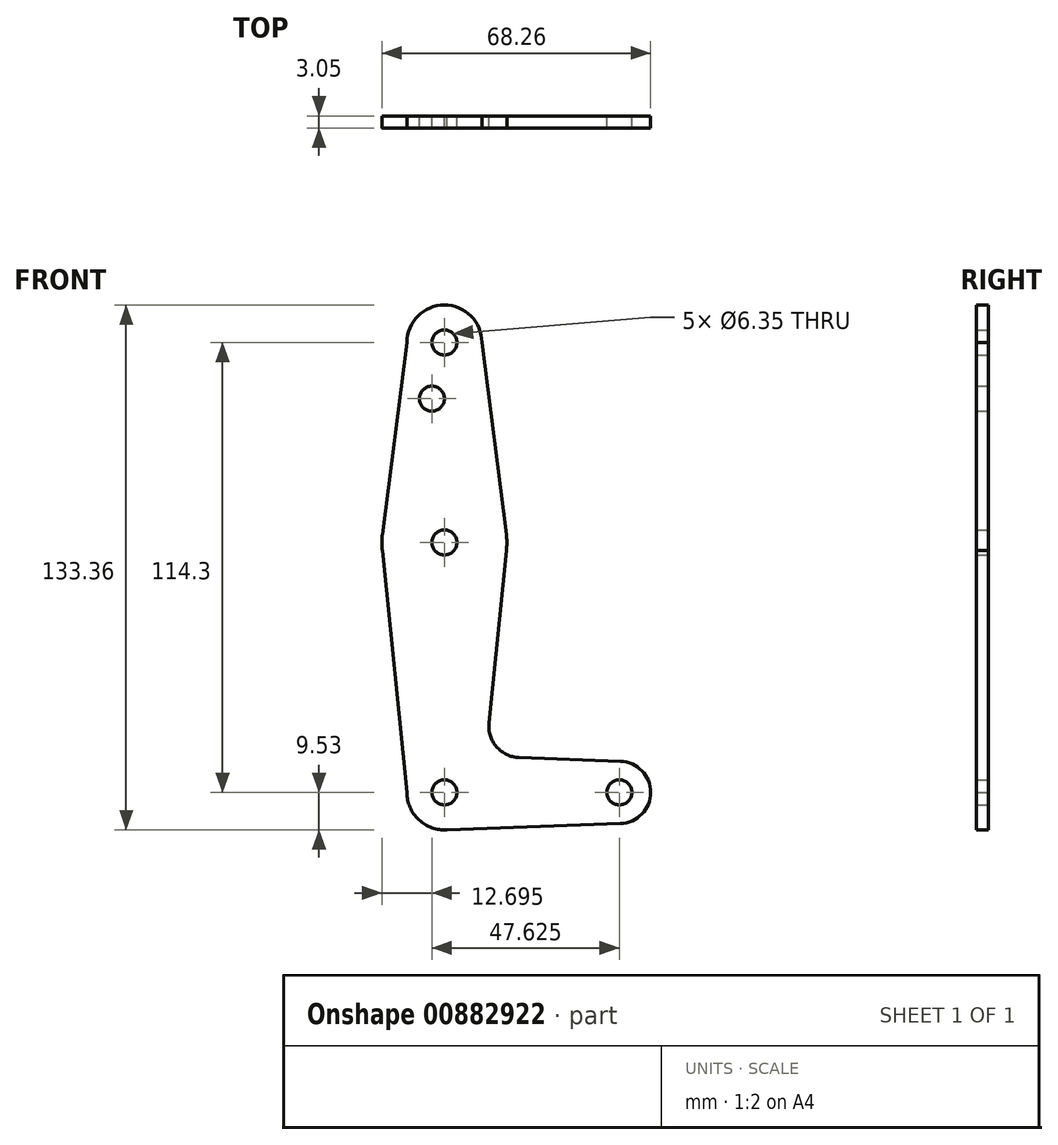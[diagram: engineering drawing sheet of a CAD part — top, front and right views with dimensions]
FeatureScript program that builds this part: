
annotation { "Feature Type Name" : "Feature", "Feature Type Description" : "" }
export const myFeature = defineFeature(function(context is Context, id is Id, definition is map)
    precondition{}
    {
        {
            var Q0;
            Q0=qCreatedBy(makeId("Front.planeOp"),FACE);
            var sketch = newSketch(context, id + "F0", { "sketchPlane" : qUnion([Q0])});
            skLineSegment(sketch, "E0", {"start": v(0, 0) * mm, "end": v(0, 114.3) * mm, "construction": true});
            skLineSegment(sketch, "E1", {"start": v(0, 0) * mm, "end": v(44.45, 0) * mm, "construction": true});
            skCircle(sketch, "E2", {"center": v(0, 63.5) * mm, "radius": 15.88 * mm});
            skCircle(sketch, "E3", {"center": v(0, 0) * mm, "radius": 9.53 * mm});
            skCircle(sketch, "E4", {"center": v(44.45, 0) * mm, "radius": 7.94 * mm});
            skCircle(sketch, "E5", {"center": v(0, 114.3) * mm, "radius": 9.53 * mm});
            skLineSegment(sketch, "E6", {"start": v(0, -9.52) * mm, "end": v(44.73, -7.93) * mm});
            skLineSegment(sketch, "E7", {"start": v(18.97, 8.85) * mm, "end": v(44.73, 7.93) * mm});
            skLineSegment(sketch, "E8", {"start": v(9.52, 114.3) * mm, "end": v(15.75, 65.5) * mm});
            skLineSegment(sketch, "E9", {"start": v(-9.52, 114.3) * mm, "end": v(-15.75, 65.5) * mm});
            skLineSegment(sketch, "E10", {"start": v(-15.75, 61.5) * mm, "end": v(-9.53, 0) * mm});
            skLineSegment(sketch, "E11", {"start": v(15.75, 61.5) * mm, "end": v(11.34, 17.6) * mm});
            skCircle(sketch, "E12", {"center": v(-3.17, 100.03) * mm, "radius": 3.18 * mm});
            skCircle(sketch, "E13", {"center": v(0, 114.3) * mm, "radius": 3.18 * mm});
            skCircle(sketch, "E14", {"center": v(0, 63.5) * mm, "radius": 3.18 * mm});
            skCircle(sketch, "E15", {"center": v(0, 0) * mm, "radius": 3.18 * mm});
            skCircle(sketch, "E16", {"center": v(44.45, 0) * mm, "radius": 3.18 * mm});
            skPoint(sketch, "E17.newPointB", {"position": v(9.57, 0) * mm});
            skArc(sketch, "E17.filletArc", {"start": v(11.34, 17.6) * mm, "mid": v(13.26, 11.57) * mm, "end": v(18.97, 8.85) * mm});
            skSolve(sketch);
        }
        {
            var Q0;
            Q0 = qSketchRegion(id + "F0", true);
            extrude(context, id + "F1", {"entities" : qUnion([Q0]), "depth" : 3.05 * mm, "offsetDistance" : 25.4 * mm});
        }
    });
